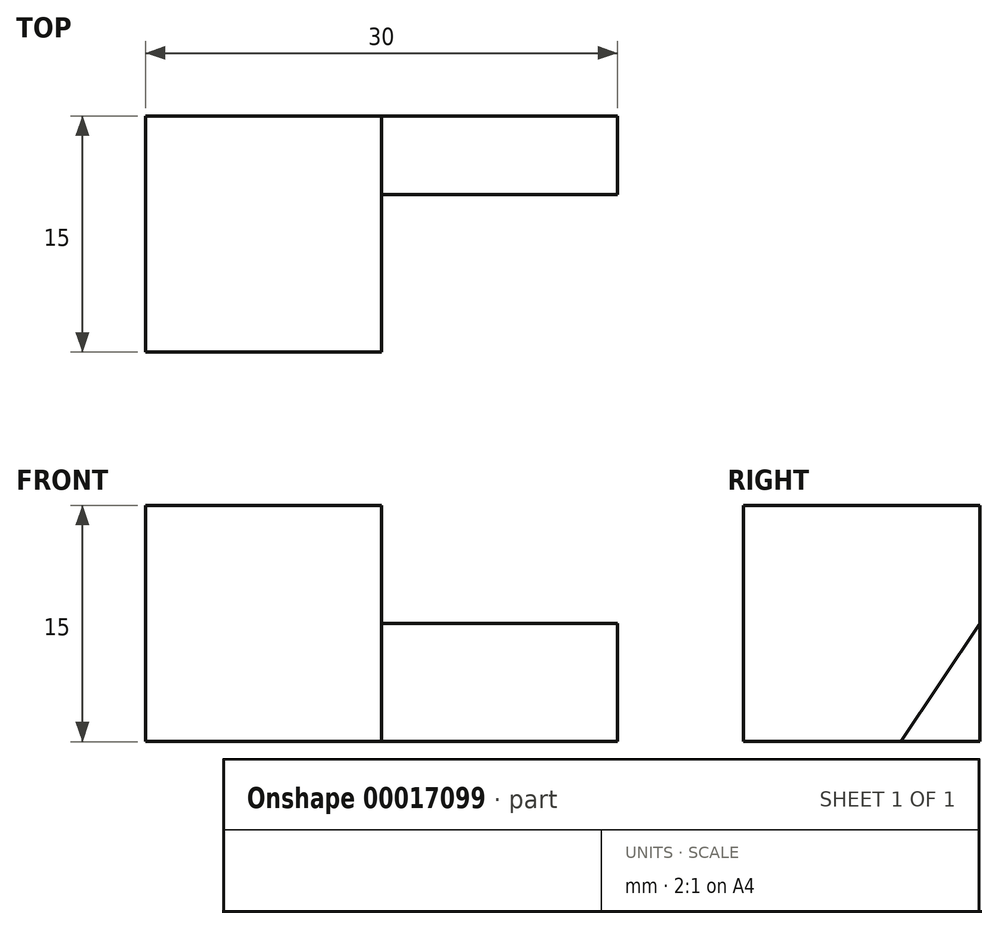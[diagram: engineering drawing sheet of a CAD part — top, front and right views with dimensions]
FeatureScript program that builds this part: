
annotation { "Feature Type Name" : "Feature", "Feature Type Description" : "" }
export const myFeature = defineFeature(function(context is Context, id is Id, definition is map)
    precondition{}
    {
        {
            var Q0;
            Q0=qCreatedBy(makeId("Right.planeOp"),FACE);
            var sketch = newSketch(context, id + "F0", { "sketchPlane" : qUnion([Q0])});
            skLineSegment(sketch, "E0.bottom", {"start": v(-14.51, 6.98) * mm, "end": v(0.49, 6.98) * mm});
            skLineSegment(sketch, "E0.top", {"start": v(-14.51, -8.02) * mm, "end": v(0.49, -8.02) * mm});
            skLineSegment(sketch, "E0.left", {"start": v(-14.51, 6.98) * mm, "end": v(-14.51, -8.02) * mm});
            skLineSegment(sketch, "E0.right", {"start": v(0.49, 6.98) * mm, "end": v(0.49, -8.02) * mm});
            skLineSegment(sketch, "E1", {"start": v(0.49, -0.52) * mm, "end": v(-4.51, -8.02) * mm});
            skSolve(sketch);
        }
        {
            var Q0;
            {var subQ0=sQuery(id+"F0.wireOp",EDGE,"E1");Q0=makeQuery(id+"F0.imprint","IMPRINT",FACE,{"disambiguationData":[TD([[makeQuery(id+"F0.imprint","IMPRINT",EDGE,{"derivedFrom":subQ0}),1.0]])]});}
            extrude(context, id + "F1", {"entities" : qUnion([Q0]), "depth" : 15 * mm});
        }
        {
            var Q0;
            {var subQ2=sQuery(id+"F0.wireOp",EDGE,"E0.bottom");Q0=makeQuery(id+"F0.imprint","IMPRINT",FACE,{"disambiguationData":[TD([[makeQuery(id+"F0.imprint","IMPRINT",EDGE,{"derivedFrom":subQ2}),-1.0]])]});}
            extrude(context, id + "F2", {"entities" : qUnion([Q0]), "oppositeDirection" : true, "depth" : 15 * mm});
        }
        {
            var Q0;
            {var subQ0=sQuery(id+"F0.wireOp",EDGE,"E1");Q0=makeQuery(id+"F0.imprint","IMPRINT",FACE,{"disambiguationData":[TD([[makeQuery(id+"F0.imprint","IMPRINT",EDGE,{"derivedFrom":subQ0}),1.0]])]});}
            extrude(context, id + "F3", {"entities" : qUnion([Q0]), "oppositeDirection" : true, "depth" : 5 * mm});
        }
        {
            var Q0;
            Q0=makeQuery(id+"F3.opExtrude","SWEPT_BODY",BODY,{"disambiguationData":[OSD([sQuery(id+"F0.wireOp",EDGE,"E0.top"),sQuery(id+"F0.wireOp",EDGE,"E0.right"),sQuery(id+"F0.wireOp",EDGE,"E1")])]});
            deleteBodies(context, id + "F4", {"entities" : qUnion([Q0])});
        }
        {
            var Q0;
            {var subQ0=sQuery(id+"F0.wireOp",EDGE,"E1");Q0=makeQuery(id+"F0.imprint","IMPRINT",FACE,{"disambiguationData":[TD([[makeQuery(id+"F0.imprint","IMPRINT",EDGE,{"derivedFrom":subQ0}),1.0]])]});}
            extrude(context, id + "F5", {"entities" : qUnion([Q0]), "operationType" : NewBodyOperationType.ADD, "oppositeDirection" : true, "depth" : 15 * mm});
        }
    });
